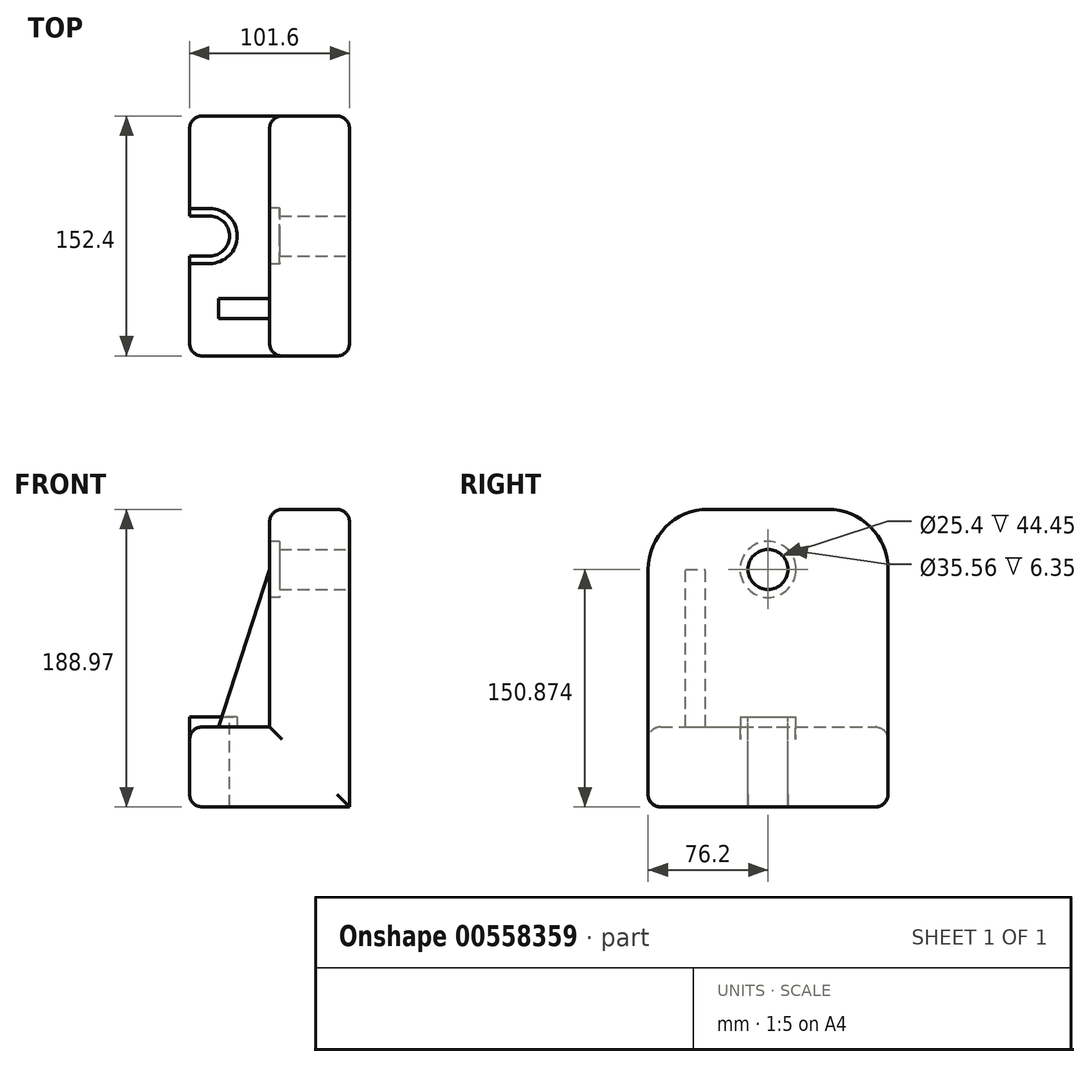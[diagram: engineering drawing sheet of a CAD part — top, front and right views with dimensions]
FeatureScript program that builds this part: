
annotation { "Feature Type Name" : "Feature", "Feature Type Description" : "" }
export const myFeature = defineFeature(function(context is Context, id is Id, definition is map)
    precondition{}
    {
        {
            var Q0;
            Q0=qCreatedBy(makeId("Front.planeOp"),FACE);
            var sketch = newSketch(context, id + "F0", { "sketchPlane" : qUnion([Q0])});
            skLineSegment(sketch, "E0.bottom", {"start": v(0, 0) * mm, "end": v(-101.6, 0) * mm});
            skLineSegment(sketch, "E0.top", {"start": v(0, 188.97) * mm, "end": v(-50.8, 188.97) * mm});
            skLineSegment(sketch, "E0.left", {"start": v(0, 0) * mm, "end": v(0, 188.97) * mm});
            skLineSegment(sketch, "E0.right", {"start": v(-101.6, 0) * mm, "end": v(-101.6, 50.8) * mm});
            skLineSegment(sketch, "E1", {"start": v(-101.6, 50.8) * mm, "end": v(-50.8, 50.8) * mm});
            skLineSegment(sketch, "E2", {"start": v(-50.8, 50.8) * mm, "end": v(-50.8, 188.97) * mm});
            skSolve(sketch);
        }
        {
            var Q0;
            Q0=makeQuery(id+"F0.imprint","IMPRINT",FACE,{"disambiguationData":[TD([[makeQuery(id+"F0.imprint","IMPRINT",EDGE,{"derivedFrom":sQuery(id+"F0.wireOp",EDGE,"E0.bottom")}),-1.0]])]});
            extrude(context, id + "F1", {"entities" : qUnion([Q0]), "endBound" : BoundingType.SYMMETRIC, "depth" : 152.4 * mm, "offsetDistance" : 25.4 * mm});
        }
        {
            var Q0;
            Q0=makeQuery(id+"F1.opExtrude","SWEPT_FACE",FACE,{"disambiguationData":[OSD([sQuery(id+"F0.wireOp",EDGE,"E0.left")])]});
            var sketch = newSketch(context, id + "F2", { "sketchPlane" : qUnion([Q0])});
            skCircle(sketch, "E3", {"center": v(0, 150.87) * mm, "radius": 12.7 * mm});
            skSolve(sketch);
        }
        {
            var Q0;
            Q0=makeQuery(id+"F2.imprint","IMPRINT",FACE,{"disambiguationData":[TD([[makeQuery(id+"F2.imprint","IMPRINT",EDGE,{"derivedFrom":sQuery(id+"F2.wireOp",EDGE,"E3")}),1.0]])]});
            extrude(context, id + "F3", {"entities" : qUnion([Q0]), "operationType" : NewBodyOperationType.REMOVE, "endBound" : BoundingType.THROUGH_ALL, "oppositeDirection" : true, "depth" : 25.4 * mm, "offsetDistance" : 25.4 * mm});
        }
        {
            var Q0;
            Q0=makeQuery(id+"F1.opExtrude","SWEPT_FACE",FACE,{"disambiguationData":[OSD([sQuery(id+"F0.wireOp",EDGE,"E1")])]});
            var sketch = newSketch(context, id + "F4", { "sketchPlane" : qUnion([Q0])});
            skLineSegment(sketch, "E4", {"start": v(-101.6, 12.7) * mm, "end": v(-88.9, 12.7) * mm});
            skLineSegment(sketch, "E5", {"start": v(-101.6, -12.7) * mm, "end": v(-88.9, -12.7) * mm});
            skPoint(sketch, "E6.center.orphan", {"position": v(-84.93, 0) * mm});
            skLineSegment(sketch, "E7", {"start": v(-101.6, 12.7) * mm, "end": v(-101.6, -12.7) * mm});
            skArc(sketch, "E8", {"start": v(-88.9, 12.7) * mm, "mid": v(-76.2, 0) * mm, "end": v(-88.9, -12.7) * mm});
            skSolve(sketch);
        }
        {
            var Q0;
            Q0=makeQuery(id+"F4.imprint","IMPRINT",FACE,{"disambiguationData":[TD([[makeQuery(id+"F4.imprint","IMPRINT",EDGE,{"derivedFrom":sQuery(id+"F4.wireOp",EDGE,"E4")}),-1.0]])]});
            extrude(context, id + "F5", {"entities" : qUnion([Q0]), "operationType" : NewBodyOperationType.REMOVE, "endBound" : BoundingType.THROUGH_ALL, "oppositeDirection" : true, "depth" : 25.4 * mm, "offsetDistance" : 25.4 * mm});
        }
        {
            var Q0;
            Q0=makeQuery(id+"F1.opExtrude","CAP_EDGE",EDGE,{"disambiguationData":[OSD([sQuery(id+"F0.wireOp",EDGE,"E0.top")])],"isStart":false});
            var Q1;
            Q1=makeQuery(id+"F1.opExtrude","CAP_EDGE",EDGE,{"disambiguationData":[OSD([sQuery(id+"F0.wireOp",EDGE,"E0.top")])],"isStart":true});
            fillet(context, id + "F6", {"entities" : qUnion([Q0, Q1]), "radius" : 38.1 * mm, "tangentPropagation" : true, "allowEdgeOverflow" : false});
        }
        {
            var Q0;
            Q0=makeQuery(id+"F1.opExtrude","SWEPT_FACE",FACE,{"disambiguationData":[OSD([sQuery(id+"F0.wireOp",EDGE,"E2")])]});
            var sketch = newSketch(context, id + "F7", { "sketchPlane" : qUnion([Q0])});
            skCircle(sketch, "E9", {"center": v(0, 150.87) * mm, "radius": 21.59 * mm});
            skCircle(sketch, "E10", {"center": v(0, 150.87) * mm, "radius": 17.78 * mm});
            skSolve(sketch);
        }
        {
            var Q0;
            Q0=makeQuery(id+"F7.imprint","IMPRINT",FACE,{"disambiguationData":[TD([[makeQuery(id+"F7.imprint","IMPRINT",EDGE,{"derivedFrom":sQuery(id+"F7.wireOp",EDGE,"E10")}),1.0]])]});
            extrude(context, id + "F8", {"entities" : qUnion([Q0]), "operationType" : NewBodyOperationType.REMOVE, "oppositeDirection" : true, "depth" : 6.35 * mm, "offsetDistance" : 25.4 * mm});
        }
        {
            var Q0;
            Q0=qCreatedBy(makeId("Front.planeOp"),FACE);
            cPlane(context, id + "F9", {"entities" : qUnion([Q0]), "cplaneType" : CPlaneType.OFFSET, "offset" : 45.97 * mm, "width" : 152.4 * mm, "height" : 152.4 * mm});
        }
        {
            var Q0;
            Q0=qCreatedBy(id+"F9.planeOp",FACE);
            var sketch = newSketch(context, id + "F10", { "sketchPlane" : qUnion([Q0])});
            skPoint(sketch, "E11.0", {"position": v(-50.8, 150.87) * mm});
            skLineSegment(sketch, "E12.0", {"start": v(-50.8, 50.8) * mm, "end": v(-50.8, 150.87) * mm});
            skLineSegment(sketch, "E12.1", {"start": v(-101.6, 50.8) * mm, "end": v(-50.8, 50.8) * mm});
            skSolve(sketch);
        }
        {
            var Q0;
            Q0=qCreatedBy(id+"F9.planeOp",FACE);
            var sketch = newSketch(context, id + "F11", { "sketchPlane" : qUnion([Q0])});
            skLineSegment(sketch, "E13.0", {"start": v(-50.8, 50.8) * mm, "end": v(-50.8, 150.87) * mm});
            skLineSegment(sketch, "E14.0", {"start": v(-101.6, 50.8) * mm, "end": v(-50.8, 50.8) * mm});
            skPoint(sketch, "E15.0", {"position": v(-50.8, 150.87) * mm});
            skPoint(sketch, "E16.0", {"position": v(-101.6, 50.8) * mm});
            skLineSegment(sketch, "E17", {"start": v(-50.8, 150.87) * mm, "end": v(-83.1, 50.8) * mm});
            skSolve(sketch);
        }
        {
            var Q0;
            {var subQ0=sQuery(id+"F11.wireOp",EDGE,"E13.0");Q0=makeQuery(id+"F11.imprint","IMPRINT",FACE,{"disambiguationData":[TD([[makeQuery(id+"F11.imprint","IMPRINT",EDGE,{"derivedFrom":subQ0}),1.0]])]});}
            extrude(context, id + "F12", {"entities" : qUnion([Q0]), "operationType" : NewBodyOperationType.ADD, "endBound" : BoundingType.SYMMETRIC, "depth" : 12.7 * mm, "offsetDistance" : 25.4 * mm});
        }
        {
            var Q0;
            Q0=makeQuery(id+"F1.opExtrude","SWEPT_FACE",FACE,{"disambiguationData":[OSD([sQuery(id+"F0.wireOp",EDGE,"E1")])]});
            var sketch = newSketch(context, id + "F13", { "sketchPlane" : qUnion([Q0])});
            skSolve(sketch);
        }
        {
            var Q0;
            {var subQ3=sQuery(id+"F0.wireOp",EDGE,"E1");Q0=makeQuery(id+"F13.imprint","IMPRINT",FACE,{"disambiguationData":[TD([[makeQuery(id+"F13.imprint","IMPRINT",EDGE,{"derivedFrom":makeQuery(id+"F1.opExtrude","CAP_EDGE",EDGE,{"disambiguationData":[OSD([subQ3])],"isStart":true})}),-1.0]])]});}
            var sketch = newSketch(context, id + "F14", { "sketchPlane" : qUnion([Q0])});
            skLineSegment(sketch, "E18.0", {"start": v(-101.6, -17.53) * mm, "end": v(-88.9, -17.53) * mm});
            skArc(sketch, "E18.1", {"start": v(-88.9, 17.53) * mm, "mid": v(-71.37, 0) * mm, "end": v(-88.9, -17.53) * mm});
            skLineSegment(sketch, "E18.2", {"start": v(-101.6, 17.53) * mm, "end": v(-88.9, 17.53) * mm});
            skSolve(sketch);
        }
        {
            var Q0;
            {var subQ3=sQuery(id+"F14.wireOp",EDGE,"E18.0");Q0=makeQuery(id+"F14.imprint","IMPRINT",FACE,{"disambiguationData":[TD([[makeQuery(id+"F14.imprint","IMPRINT",EDGE,{"derivedFrom":subQ3}),1.0]])]});}
            extrude(context, id + "F15", {"entities" : qUnion([Q0]), "operationType" : NewBodyOperationType.ADD, "depth" : 6.35 * mm, "offsetDistance" : 25.4 * mm});
        }
        {
            var Q0;
            Q0=makeQuery(id+"F1.opExtrude","CAP_EDGE",EDGE,{"disambiguationData":[OSD([sQuery(id+"F0.wireOp",EDGE,"E1")])],"isStart":false});
            var Q1;
            Q1=makeQuery(id+"F1.opExtrude","CAP_EDGE",EDGE,{"disambiguationData":[OSD([sQuery(id+"F0.wireOp",EDGE,"E1")])],"isStart":true});
            var Q2;
            Q2=makeQuery(id+"F1.opExtrude","CAP_EDGE",EDGE,{"disambiguationData":[OSD([sQuery(id+"F0.wireOp",EDGE,"E0.bottom")])],"isStart":false});
            var Q3;
            Q3=makeQuery(id+"F1.opExtrude","CAP_FACE",FACE,{"disambiguationData":[OSD([sQuery(id+"F0.wireOp",EDGE,"E0.bottom"),sQuery(id+"F0.wireOp",EDGE,"E0.top"),sQuery(id+"F0.wireOp",EDGE,"E0.left"),sQuery(id+"F0.wireOp",EDGE,"E0.right"),sQuery(id+"F0.wireOp",EDGE,"E1"),sQuery(id+"F0.wireOp",EDGE,"E2")])],"isStart":false});
            var Q4;
            Q4=makeQuery(id+"F1.opExtrude","CAP_EDGE",EDGE,{"disambiguationData":[OSD([sQuery(id+"F0.wireOp",EDGE,"E0.bottom")])],"isStart":true});
            var Q5;
            Q5=makeQuery(id+"F1.opExtrude","CAP_EDGE",EDGE,{"disambiguationData":[OSD([sQuery(id+"F0.wireOp",EDGE,"E0.right")])],"isStart":true});
            var Q6;
            {var subQ0=sQuery(id+"F0.wireOp",EDGE,"E1");var subQ1=sQuery(id+"F0.wireOp",EDGE,"E0.right");Q6=makeQuery(id+"F5.boolean.opBoolean","SPLIT",EDGE,{"disambiguationData":[TD([makeQuery(id+"F5.opExtrude","SWEPT_FACE",FACE,{"disambiguationData":[OSD([sQuery(id+"F4.wireOp",EDGE,"E4")])]})])],"derivedFrom":makeQuery(id+"F1.opExtrude","SWEPT_EDGE",EDGE,{"disambiguationData":[OSD([subQ1,subQ0])]})});}
            var Q7;
            {var subQ0=sQuery(id+"F0.wireOp",EDGE,"E1");var subQ1=sQuery(id+"F0.wireOp",EDGE,"E0.right");Q7=makeQuery(id+"F5.boolean.opBoolean","SPLIT",EDGE,{"disambiguationData":[TD([makeQuery(id+"F5.opExtrude","SWEPT_FACE",FACE,{"disambiguationData":[OSD([sQuery(id+"F4.wireOp",EDGE,"E5")])]})])],"derivedFrom":makeQuery(id+"F1.opExtrude","SWEPT_EDGE",EDGE,{"disambiguationData":[OSD([subQ1,subQ0])]})});}
            var Q8;
            {var subQ0=sQuery(id+"F0.wireOp",EDGE,"E0.bottom");var subQ1=sQuery(id+"F0.wireOp",EDGE,"E0.right");Q8=makeQuery(id+"F5.boolean.opBoolean","SPLIT",EDGE,{"disambiguationData":[TD([makeQuery(id+"F5.opExtrude","SWEPT_FACE",FACE,{"disambiguationData":[OSD([sQuery(id+"F4.wireOp",EDGE,"E5")])]})])],"derivedFrom":makeQuery(id+"F1.opExtrude","SWEPT_EDGE",EDGE,{"disambiguationData":[OSD([subQ0,subQ1])]})});}
            var Q9;
            {var subQ0=sQuery(id+"F0.wireOp",EDGE,"E0.bottom");var subQ1=sQuery(id+"F0.wireOp",EDGE,"E0.right");Q9=makeQuery(id+"F5.boolean.opBoolean","SPLIT",EDGE,{"disambiguationData":[TD([makeQuery(id+"F5.opExtrude","SWEPT_FACE",FACE,{"disambiguationData":[OSD([sQuery(id+"F4.wireOp",EDGE,"E4")])]})])],"derivedFrom":makeQuery(id+"F1.opExtrude","SWEPT_EDGE",EDGE,{"disambiguationData":[OSD([subQ0,subQ1])]})});}
            fillet(context, id + "F16", {"entities" : qUnion([Q0, Q1, Q2, Q3, Q4, Q5, Q6, Q7, Q8, Q9]), "radius" : 7.97 * mm, "tangentPropagation" : true, "allowEdgeOverflow" : false});
        }
    });
